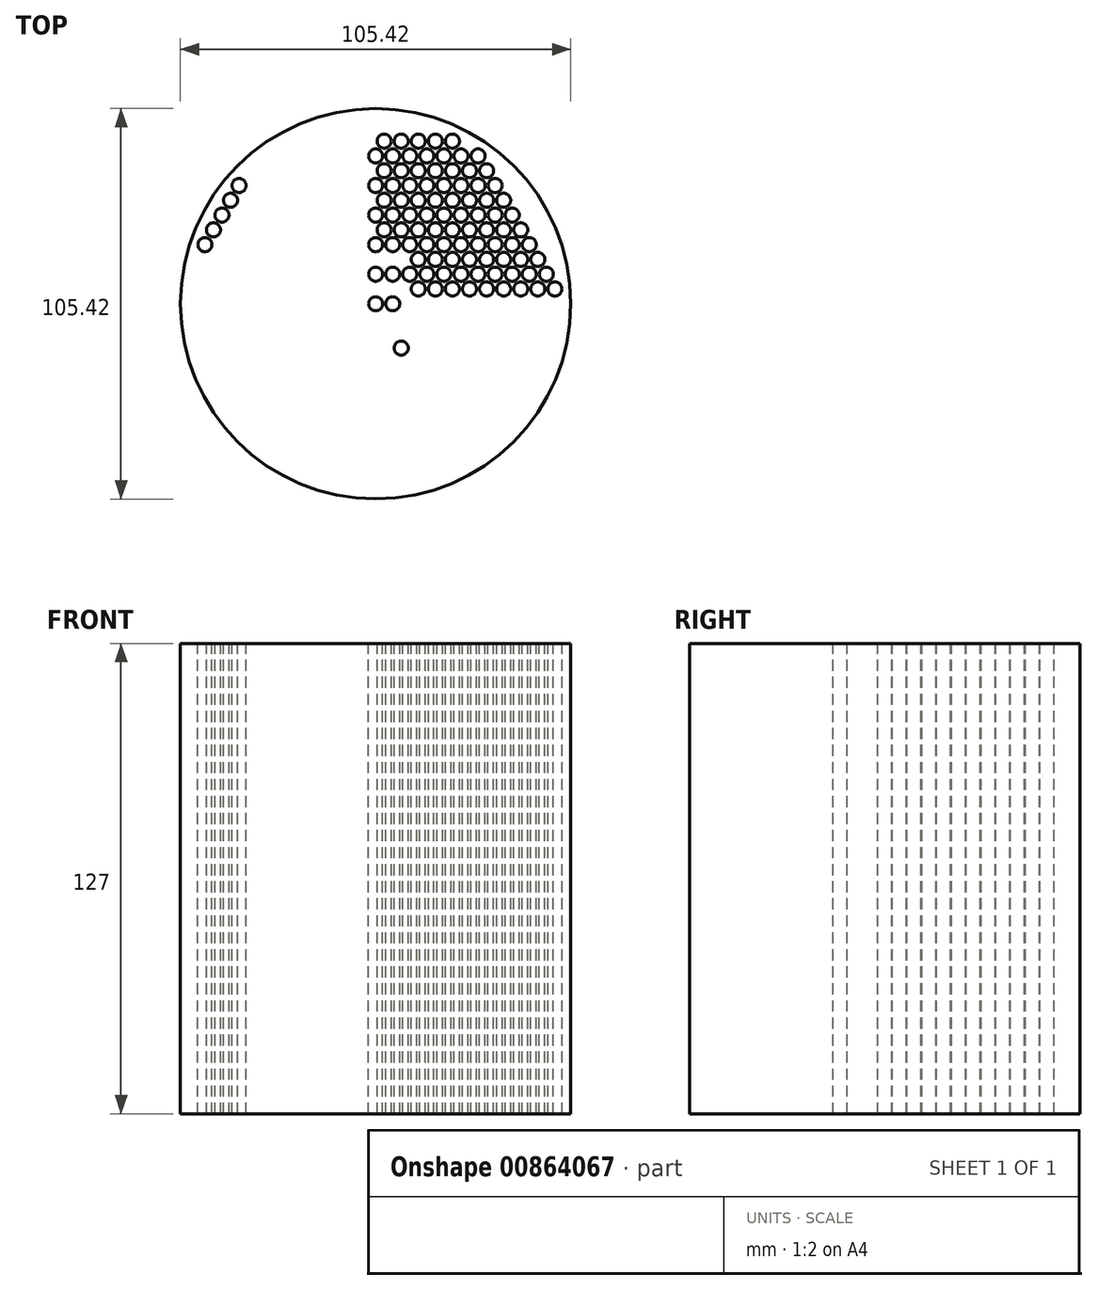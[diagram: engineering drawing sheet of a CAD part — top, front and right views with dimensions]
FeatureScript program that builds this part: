
annotation { "Feature Type Name" : "Feature", "Feature Type Description" : "" }
export const myFeature = defineFeature(function(context is Context, id is Id, definition is map)
    precondition{}
    {
        {
            var Q0;
            Q0=qCreatedBy(makeId("Top.planeOp"),FACE);
            var sketch = newSketch(context, id + "F0", { "sketchPlane" : qUnion([Q0])});
            skCircle(sketch, "E0", {"center": v(0, 0) * mm, "radius": 52.7 * mm});
            skSolve(sketch);
        }
        {
            var Q0;
            Q0=makeQuery(id+"F0.imprint","IMPRINT",FACE,{"disambiguationData":[TD([[makeQuery(id+"F0.imprint","IMPRINT",EDGE,{"derivedFrom":sQuery(id+"F0.wireOp",EDGE,"E0")}),1.0]])]});
            extrude(context, id + "F1", {"entities" : qUnion([Q0]), "depth" : 127 * mm, "offsetDistance" : 25.4 * mm});
        }
        {
            var Q0;
            Q0=makeQuery(id+"F1.opExtrude","CAP_FACE",FACE,{"disambiguationData":[OSD([sQuery(id+"F0.wireOp",EDGE,"E0")])],"isStart":false});
            var sketch = newSketch(context, id + "F2", { "sketchPlane" : qUnion([Q0])});
            skCircle(sketch, "E1", {"center": v(0, 0) * mm, "radius": 50.8 * mm});
            skCircle(sketch, "E2", {"center": v(0, 0) * mm, "radius": 1.9 * mm});
            skSolve(sketch);
        }
        {
            var Q0;
            Q0=makeQuery(id+"F2.imprint","IMPRINT",FACE,{"disambiguationData":[TD([[makeQuery(id+"F2.imprint","IMPRINT",EDGE,{"derivedFrom":sQuery(id+"F2.wireOp",EDGE,"E2")}),1.0]])]});
            var Q1;
            Q1=makeQuery(id+"F1.opExtrude","CAP_FACE",FACE,{"disambiguationData":[OSD([sQuery(id+"F0.wireOp",EDGE,"E0")])],"isStart":true});
            extrude(context, id + "F3", {"entities" : qUnion([Q0]), "operationType" : NewBodyOperationType.REMOVE, "endBound" : BoundingType.UP_TO_SURFACE, "oppositeDirection" : true, "depth" : 25.4 * mm, "endBoundEntityFace" : qUnion([Q1]), "offsetDistance" : 25.4 * mm});
        }
        {
            var Q0;
            Q0=makeQuery(id+"F1.opExtrude","CAP_FACE",FACE,{"disambiguationData":[OSD([sQuery(id+"F0.wireOp",EDGE,"E0")])],"isStart":false});
            var sketch = newSketch(context, id + "F4", { "sketchPlane" : qUnion([Q0])});
            skLineSegment(sketch, "E3", {"start": v(0, 0) * mm, "end": v(52.7, 0) * mm});
            skCircle(sketch, "E4", {"center": v(4.6, 0) * mm, "radius": 1.9 * mm});
            skSolve(sketch);
        }
        {
            var Q0;
            Q0=qCreatedBy(makeId("Front.planeOp"),FACE);
            var sketch = newSketch(context, id + "F5", { "sketchPlane" : qUnion([Q0])});
            skLineSegment(sketch, "E5", {"start": v(0, 162.67) * mm, "end": v(0, -94.61) * mm});
            skSolve(sketch);
        }
        {
            var Q0;
            {var subQ0=sQuery(id+"F4.wireOp",EDGE,"E4");var subQ1=sQuery(id+"F4.wireOp",EDGE,"E3");var subQ2=makeQuery(id+"F4.imprint","INTERSECT",VERTEX,{"disambiguationData":[OD(0.0)],"derivedFrom":[subQ1,subQ0]});Q0=makeQuery(id+"F4.imprint","IMPRINT",FACE,{"disambiguationData":[TD([[makeQuery(id+"F4.imprint","IMPRINT",EDGE,{"disambiguationData":[TD([[subQ2,-1.0]])],"derivedFrom":subQ1}),1.0]])]});}
            var Q1;
            {var subQ0=sQuery(id+"F4.wireOp",EDGE,"E4");var subQ1=sQuery(id+"F4.wireOp",EDGE,"E3");var subQ2=makeQuery(id+"F4.imprint","INTERSECT",VERTEX,{"disambiguationData":[OD(0.0)],"derivedFrom":[subQ1,subQ0]});Q1=makeQuery(id+"F4.imprint","IMPRINT",FACE,{"disambiguationData":[TD([[makeQuery(id+"F4.imprint","IMPRINT",EDGE,{"disambiguationData":[TD([[subQ2,-1.0]])],"derivedFrom":subQ1}),-1.0]])]});}
            var Q2;
            Q2=makeQuery(id+"F1.opExtrude","CAP_FACE",FACE,{"disambiguationData":[OSD([sQuery(id+"F0.wireOp",EDGE,"E0")])],"isStart":true});
            extrude(context, id + "F6", {"entities" : qUnion([Q0, Q1]), "operationType" : NewBodyOperationType.REMOVE, "endBound" : BoundingType.UP_TO_SURFACE, "oppositeDirection" : true, "depth" : 25.4 * mm, "endBoundEntityFace" : qUnion([Q2]), "offsetDistance" : 25.4 * mm});
        }
        {
            var Q0;
            Q0=makeQuery(id+"F1.opExtrude","CAP_FACE",FACE,{"disambiguationData":[OSD([sQuery(id+"F0.wireOp",EDGE,"E0")])],"isStart":false});
            var sketch = newSketch(context, id + "F7", { "sketchPlane" : qUnion([Q0])});
            skLineSegment(sketch, "E6", {"start": v(0, 0) * mm, "end": v(0, 7.98) * mm});
            skCircle(sketch, "E7", {"center": v(0, 7.98) * mm, "radius": 1.9 * mm});
            skSolve(sketch);
        }
        {
            var Q0;
            Q0=makeQuery(id+"F7.imprint","IMPRINT",FACE,{"disambiguationData":[TD([[makeQuery(id+"F7.imprint","IMPRINT",EDGE,{"derivedFrom":sQuery(id+"F7.wireOp",EDGE,"E7")}),1.0]])]});
            var Q1;
            Q1=makeQuery(id+"F1.opExtrude","CAP_FACE",FACE,{"disambiguationData":[OSD([sQuery(id+"F0.wireOp",EDGE,"E0")])],"isStart":true});
            extrude(context, id + "F8", {"entities" : qUnion([Q0]), "operationType" : NewBodyOperationType.REMOVE, "endBound" : BoundingType.UP_TO_SURFACE, "oppositeDirection" : true, "depth" : 25.4 * mm, "endBoundEntityFace" : qUnion([Q1]), "offsetDistance" : 25.4 * mm});
        }
        {
            var Q0;
            Q0=makeQuery(id+"F1.opExtrude","CAP_FACE",FACE,{"disambiguationData":[OSD([sQuery(id+"F0.wireOp",EDGE,"E0")])],"isStart":false});
            var sketch = newSketch(context, id + "F9", { "sketchPlane" : qUnion([Q0])});
            skLineSegment(sketch, "E8", {"start": v(0, 0) * mm, "end": v(8.77, 15.2) * mm});
            skCircle(sketch, "E9", {"center": v(4.61, 7.98) * mm, "radius": 1.9 * mm});
            skSolve(sketch);
        }
        {
            var Q0;
            {var subQ0=sQuery(id+"F9.wireOp",EDGE,"E9");var subQ1=sQuery(id+"F9.wireOp",EDGE,"E8");var subQ2=makeQuery(id+"F9.imprint","INTERSECT",VERTEX,{"disambiguationData":[OD(0.0)],"derivedFrom":[subQ1,subQ0]});Q0=makeQuery(id+"F9.imprint","IMPRINT",FACE,{"disambiguationData":[TD([[makeQuery(id+"F9.imprint","IMPRINT",EDGE,{"disambiguationData":[TD([[subQ2,-1.0]])],"derivedFrom":subQ1}),-1.0]])]});}
            var Q1;
            {var subQ0=sQuery(id+"F9.wireOp",EDGE,"E9");var subQ1=sQuery(id+"F9.wireOp",EDGE,"E8");var subQ2=makeQuery(id+"F9.imprint","INTERSECT",VERTEX,{"disambiguationData":[OD(0.0)],"derivedFrom":[subQ1,subQ0]});Q1=makeQuery(id+"F9.imprint","IMPRINT",FACE,{"disambiguationData":[TD([[makeQuery(id+"F9.imprint","IMPRINT",EDGE,{"disambiguationData":[TD([[subQ2,-1.0]])],"derivedFrom":subQ1}),1.0]])]});}
            var Q2;
            Q2=makeQuery(id+"F1.opExtrude","CAP_FACE",FACE,{"disambiguationData":[OSD([sQuery(id+"F0.wireOp",EDGE,"E0")])],"isStart":true});
            extrude(context, id + "F10", {"entities" : qUnion([Q0, Q1]), "operationType" : NewBodyOperationType.REMOVE, "endBound" : BoundingType.UP_TO_SURFACE, "oppositeDirection" : true, "depth" : 25.4 * mm, "endBoundEntityFace" : qUnion([Q2]), "offsetDistance" : 25.4 * mm});
        }
        {
            var Q0;
            Q0=makeQuery(id+"F1.opExtrude","CAP_FACE",FACE,{"disambiguationData":[OSD([sQuery(id+"F0.wireOp",EDGE,"E0")])],"isStart":false});
            var sketch = newSketch(context, id + "F11", { "sketchPlane" : qUnion([Q0])});
            skLineSegment(sketch, "E10", {"start": v(0, 0) * mm, "end": v(9.22, 7.98) * mm});
            skCircle(sketch, "E11", {"center": v(9.22, 7.98) * mm, "radius": 1.9 * mm});
            skSolve(sketch);
        }
        {
            var Q0;
            Q0=makeQuery(id+"F11.imprint","IMPRINT",FACE,{"disambiguationData":[TD([[makeQuery(id+"F11.imprint","IMPRINT",EDGE,{"derivedFrom":sQuery(id+"F11.wireOp",EDGE,"E11")}),1.0]])]});
            var Q1;
            Q1=makeQuery(id+"F1.opExtrude","CAP_FACE",FACE,{"disambiguationData":[OSD([sQuery(id+"F0.wireOp",EDGE,"E0")])],"isStart":true});
            extrude(context, id + "F12", {"entities" : qUnion([Q0]), "operationType" : NewBodyOperationType.REMOVE, "endBound" : BoundingType.UP_TO_SURFACE, "oppositeDirection" : true, "depth" : 25.4 * mm, "endBoundEntityFace" : qUnion([Q1]), "offsetDistance" : 25.4 * mm});
        }
        {
            var Q0;
            Q0=makeQuery(id+"F1.opExtrude","CAP_FACE",FACE,{"disambiguationData":[OSD([sQuery(id+"F0.wireOp",EDGE,"E0")])],"isStart":false});
            var sketch = newSketch(context, id + "F13", { "sketchPlane" : qUnion([Q0])});
            skLineSegment(sketch, "E12", {"start": v(0, 0) * mm, "end": v(11.53, 4) * mm});
            skCircle(sketch, "E13", {"center": v(11.53, 4) * mm, "radius": 1.9 * mm});
            skSolve(sketch);
        }
        {
            var Q0;
            Q0=makeQuery(id+"F13.imprint","IMPRINT",FACE,{"disambiguationData":[TD([[makeQuery(id+"F13.imprint","IMPRINT",EDGE,{"derivedFrom":sQuery(id+"F13.wireOp",EDGE,"E13")}),1.0]])]});
            var Q1;
            Q1=makeQuery(id+"F1.opExtrude","CAP_FACE",FACE,{"disambiguationData":[OSD([sQuery(id+"F0.wireOp",EDGE,"E0")])],"isStart":true});
            extrude(context, id + "F14", {"entities" : qUnion([Q0]), "operationType" : NewBodyOperationType.REMOVE, "endBound" : BoundingType.UP_TO_SURFACE, "oppositeDirection" : true, "depth" : 25.4 * mm, "endBoundEntityFace" : qUnion([Q1]), "offsetDistance" : 25.4 * mm});
        }
        {
            var Q0;
            Q0=makeQuery(id+"F1.opExtrude","CAP_FACE",FACE,{"disambiguationData":[OSD([sQuery(id+"F0.wireOp",EDGE,"E0")])],"isStart":false});
            var sketch = newSketch(context, id + "F15", { "sketchPlane" : qUnion([Q0])});
            skLineSegment(sketch, "E14", {"start": v(0, 0) * mm, "end": v(6.92, -11.98) * mm});
            skCircle(sketch, "E15", {"center": v(6.92, -11.98) * mm, "radius": 1.9 * mm});
            skSolve(sketch);
        }
        {
            var Q0;
            Q0=makeQuery(id+"F15.imprint","IMPRINT",FACE,{"disambiguationData":[TD([[makeQuery(id+"F15.imprint","IMPRINT",EDGE,{"derivedFrom":sQuery(id+"F15.wireOp",EDGE,"E15")}),1.0]])]});
            var Q1;
            Q1=makeQuery(id+"F1.opExtrude","CAP_FACE",FACE,{"disambiguationData":[OSD([sQuery(id+"F0.wireOp",EDGE,"E0")])],"isStart":true});
            extrude(context, id + "F16", {"entities" : qUnion([Q0]), "operationType" : NewBodyOperationType.REMOVE, "endBound" : BoundingType.UP_TO_SURFACE, "oppositeDirection" : true, "depth" : 25.4 * mm, "endBoundEntityFace" : qUnion([Q1]), "offsetDistance" : 25.4 * mm});
        }
        {
            var Q0;
            Q0=makeQuery(id+"F1.opExtrude","CAP_FACE",FACE,{"disambiguationData":[OSD([sQuery(id+"F0.wireOp",EDGE,"E0")])],"isStart":false});
            var sketch = newSketch(context, id + "F17", { "sketchPlane" : qUnion([Q0])});
            skLineSegment(sketch, "E16", {"start": v(0, 0) * mm, "end": v(0, 15.97) * mm});
            skLineSegment(sketch, "E17", {"start": v(0, 0) * mm, "end": v(4.6, 15.97) * mm});
            skCircle(sketch, "E18", {"center": v(0, 15.97) * mm, "radius": 1.9 * mm});
            skCircle(sketch, "E19", {"center": v(4.6, 15.97) * mm, "radius": 1.9 * mm});
            skLineSegment(sketch, "E20", {"start": v(0, 0) * mm, "end": v(9.22, 15.97) * mm});
            skCircle(sketch, "E21", {"center": v(9.22, 15.97) * mm, "radius": 1.9 * mm});
            skLineSegment(sketch, "E22", {"start": v(0, 0) * mm, "end": v(11.52, 11.98) * mm});
            skCircle(sketch, "E23", {"center": v(11.52, 11.98) * mm, "radius": 1.9 * mm});
            skLineSegment(sketch, "E24", {"start": v(0, 0) * mm, "end": v(13.83, 7.98) * mm});
            skCircle(sketch, "E25", {"center": v(13.83, 7.98) * mm, "radius": 1.9 * mm});
            skLineSegment(sketch, "E26", {"start": v(0, 0) * mm, "end": v(16.14, 4) * mm});
            skCircle(sketch, "E27", {"center": v(16.14, 4) * mm, "radius": 1.9 * mm});
            skSolve(sketch);
        }
        {
            var Q0;
            Q0=makeQuery(id+"F17.imprint","IMPRINT",FACE,{"disambiguationData":[TD([[makeQuery(id+"F17.imprint","IMPRINT",EDGE,{"derivedFrom":sQuery(id+"F17.wireOp",EDGE,"E18")}),1.0]])]});
            var Q1;
            Q1=makeQuery(id+"F17.imprint","IMPRINT",FACE,{"disambiguationData":[TD([[makeQuery(id+"F17.imprint","IMPRINT",EDGE,{"derivedFrom":sQuery(id+"F17.wireOp",EDGE,"E19")}),1.0]])]});
            var Q2;
            Q2=makeQuery(id+"F17.imprint","IMPRINT",FACE,{"disambiguationData":[TD([[makeQuery(id+"F17.imprint","IMPRINT",EDGE,{"derivedFrom":sQuery(id+"F17.wireOp",EDGE,"E21")}),1.0]])]});
            var Q3;
            Q3=makeQuery(id+"F17.imprint","IMPRINT",FACE,{"disambiguationData":[TD([[makeQuery(id+"F17.imprint","IMPRINT",EDGE,{"derivedFrom":sQuery(id+"F17.wireOp",EDGE,"E23")}),1.0]])]});
            var Q4;
            Q4=makeQuery(id+"F17.imprint","IMPRINT",FACE,{"disambiguationData":[TD([[makeQuery(id+"F17.imprint","IMPRINT",EDGE,{"derivedFrom":sQuery(id+"F17.wireOp",EDGE,"E25")}),1.0]])]});
            var Q5;
            Q5=makeQuery(id+"F17.imprint","IMPRINT",FACE,{"disambiguationData":[TD([[makeQuery(id+"F17.imprint","IMPRINT",EDGE,{"derivedFrom":sQuery(id+"F17.wireOp",EDGE,"E27")}),1.0]])]});
            var Q6;
            Q6=makeQuery(id+"F1.opExtrude","CAP_FACE",FACE,{"disambiguationData":[OSD([sQuery(id+"F0.wireOp",EDGE,"E0")])],"isStart":true});
            extrude(context, id + "F18", {"entities" : qUnion([Q0, Q1, Q2, Q3, Q4, Q5]), "operationType" : NewBodyOperationType.REMOVE, "endBound" : BoundingType.UP_TO_SURFACE, "oppositeDirection" : true, "depth" : 25.4 * mm, "endBoundEntityFace" : qUnion([Q6]), "offsetDistance" : 25.4 * mm});
        }
        {
            var Q0;
            Q0=makeQuery(id+"F1.opExtrude","CAP_FACE",FACE,{"disambiguationData":[OSD([sQuery(id+"F0.wireOp",EDGE,"E0")])],"isStart":false});
            var sketch = newSketch(context, id + "F19", { "sketchPlane" : qUnion([Q0])});
            skLineSegment(sketch, "E28", {"start": v(0, 0) * mm, "end": v(2.3, 19.96) * mm});
            skCircle(sketch, "E29", {"center": v(2.3, 19.96) * mm, "radius": 1.9 * mm});
            skLineSegment(sketch, "E30", {"start": v(0, 0) * mm, "end": v(6.91, 19.96) * mm});
            skCircle(sketch, "E31", {"center": v(6.91, 19.96) * mm, "radius": 1.9 * mm});
            skLineSegment(sketch, "E32", {"start": v(0, 0) * mm, "end": v(11.52, 19.96) * mm});
            skCircle(sketch, "E33", {"center": v(11.52, 19.96) * mm, "radius": 1.9 * mm});
            skLineSegment(sketch, "E34", {"start": v(0, 0) * mm, "end": v(13.83, 15.97) * mm});
            skCircle(sketch, "E35", {"center": v(13.83, 15.97) * mm, "radius": 1.9 * mm});
            skLineSegment(sketch, "E36", {"start": v(0, 0) * mm, "end": v(16.13, 11.98) * mm});
            skCircle(sketch, "E37", {"center": v(16.13, 11.98) * mm, "radius": 1.9 * mm});
            skLineSegment(sketch, "E38", {"start": v(0, 0) * mm, "end": v(18.44, 7.98) * mm});
            skCircle(sketch, "E39", {"center": v(18.44, 7.98) * mm, "radius": 1.9 * mm});
            skLineSegment(sketch, "E40", {"start": v(0, 0) * mm, "end": v(20.75, 4) * mm});
            skCircle(sketch, "E41", {"center": v(20.75, 4) * mm, "radius": 1.9 * mm});
            skSolve(sketch);
        }
        {
            var Q0;
            Q0=makeQuery(id+"F19.imprint","IMPRINT",FACE,{"disambiguationData":[TD([[makeQuery(id+"F19.imprint","IMPRINT",EDGE,{"derivedFrom":sQuery(id+"F19.wireOp",EDGE,"E29")}),1.0]])]});
            var Q1;
            Q1=makeQuery(id+"F19.imprint","IMPRINT",FACE,{"disambiguationData":[TD([[makeQuery(id+"F19.imprint","IMPRINT",EDGE,{"derivedFrom":sQuery(id+"F19.wireOp",EDGE,"E31")}),1.0]])]});
            var Q2;
            Q2=makeQuery(id+"F19.imprint","IMPRINT",FACE,{"disambiguationData":[TD([[makeQuery(id+"F19.imprint","IMPRINT",EDGE,{"derivedFrom":sQuery(id+"F19.wireOp",EDGE,"E33")}),1.0]])]});
            var Q3;
            Q3=makeQuery(id+"F19.imprint","IMPRINT",FACE,{"disambiguationData":[TD([[makeQuery(id+"F19.imprint","IMPRINT",EDGE,{"derivedFrom":sQuery(id+"F19.wireOp",EDGE,"E35")}),1.0]])]});
            var Q4;
            Q4=makeQuery(id+"F19.imprint","IMPRINT",FACE,{"disambiguationData":[TD([[makeQuery(id+"F19.imprint","IMPRINT",EDGE,{"derivedFrom":sQuery(id+"F19.wireOp",EDGE,"E37")}),1.0]])]});
            var Q5;
            Q5=makeQuery(id+"F19.imprint","IMPRINT",FACE,{"disambiguationData":[TD([[makeQuery(id+"F19.imprint","IMPRINT",EDGE,{"derivedFrom":sQuery(id+"F19.wireOp",EDGE,"E39")}),1.0]])]});
            var Q6;
            Q6=makeQuery(id+"F19.imprint","IMPRINT",FACE,{"disambiguationData":[TD([[makeQuery(id+"F19.imprint","IMPRINT",EDGE,{"derivedFrom":sQuery(id+"F19.wireOp",EDGE,"E41")}),1.0]])]});
            var Q7;
            Q7=makeQuery(id+"F1.opExtrude","CAP_FACE",FACE,{"disambiguationData":[OSD([sQuery(id+"F0.wireOp",EDGE,"E0")])],"isStart":true});
            extrude(context, id + "F20", {"entities" : qUnion([Q0, Q1, Q2, Q3, Q4, Q5, Q6]), "operationType" : NewBodyOperationType.REMOVE, "endBound" : BoundingType.UP_TO_SURFACE, "oppositeDirection" : true, "depth" : 25.4 * mm, "endBoundEntityFace" : qUnion([Q7]), "offsetDistance" : 25.4 * mm});
        }
        {
            var Q0;
            Q0=makeQuery(id+"F1.opExtrude","CAP_FACE",FACE,{"disambiguationData":[OSD([sQuery(id+"F0.wireOp",EDGE,"E0")])],"isStart":false});
            var sketch = newSketch(context, id + "F21", { "sketchPlane" : qUnion([Q0])});
            skLineSegment(sketch, "E42", {"start": v(0, 0) * mm, "end": v(0, 23.95) * mm});
            skLineSegment(sketch, "E43", {"start": v(0, 0) * mm, "end": v(4.6, 23.95) * mm});
            skLineSegment(sketch, "E44", {"start": v(0, 0) * mm, "end": v(9.22, 23.95) * mm});
            skCircle(sketch, "E45", {"center": v(0, 23.95) * mm, "radius": 1.9 * mm});
            skCircle(sketch, "E46", {"center": v(4.6, 23.95) * mm, "radius": 1.9 * mm});
            skCircle(sketch, "E47", {"center": v(9.22, 23.95) * mm, "radius": 1.9 * mm});
            skLineSegment(sketch, "E48", {"start": v(0, 0) * mm, "end": v(13.83, 23.95) * mm});
            skLineSegment(sketch, "E49", {"start": v(0, 0) * mm, "end": v(16.13, 19.96) * mm});
            skLineSegment(sketch, "E50", {"start": v(0, 0) * mm, "end": v(18.44, 15.97) * mm});
            skLineSegment(sketch, "E51", {"start": v(0, 0) * mm, "end": v(20.74, 11.98) * mm});
            skLineSegment(sketch, "E52", {"start": v(0, 0) * mm, "end": v(23.05, 7.98) * mm});
            skLineSegment(sketch, "E53", {"start": v(0, 0) * mm, "end": v(25.36, 4) * mm});
            skCircle(sketch, "E54", {"center": v(13.83, 23.95) * mm, "radius": 1.9 * mm});
            skCircle(sketch, "E55", {"center": v(16.13, 19.96) * mm, "radius": 1.9 * mm});
            skCircle(sketch, "E56", {"center": v(18.44, 15.97) * mm, "radius": 1.9 * mm});
            skCircle(sketch, "E57", {"center": v(20.74, 11.98) * mm, "radius": 1.9 * mm});
            skCircle(sketch, "E58", {"center": v(23.05, 7.98) * mm, "radius": 1.9 * mm});
            skCircle(sketch, "E59", {"center": v(25.36, 4) * mm, "radius": 1.9 * mm});
            skSolve(sketch);
        }
        {
            var Q0;
            Q0=makeQuery(id+"F21.imprint","IMPRINT",FACE,{"disambiguationData":[TD([[makeQuery(id+"F21.imprint","IMPRINT",EDGE,{"derivedFrom":sQuery(id+"F21.wireOp",EDGE,"E45")}),1.0]])]});
            var Q1;
            Q1=makeQuery(id+"F21.imprint","IMPRINT",FACE,{"disambiguationData":[TD([[makeQuery(id+"F21.imprint","IMPRINT",EDGE,{"derivedFrom":sQuery(id+"F21.wireOp",EDGE,"E46")}),1.0]])]});
            var Q2;
            Q2=makeQuery(id+"F21.imprint","IMPRINT",FACE,{"disambiguationData":[TD([[makeQuery(id+"F21.imprint","IMPRINT",EDGE,{"derivedFrom":sQuery(id+"F21.wireOp",EDGE,"E47")}),1.0]])]});
            var Q3;
            Q3=makeQuery(id+"F21.imprint","IMPRINT",FACE,{"disambiguationData":[TD([[makeQuery(id+"F21.imprint","IMPRINT",EDGE,{"derivedFrom":sQuery(id+"F21.wireOp",EDGE,"E54")}),1.0]])]});
            var Q4;
            Q4=makeQuery(id+"F21.imprint","IMPRINT",FACE,{"disambiguationData":[TD([[makeQuery(id+"F21.imprint","IMPRINT",EDGE,{"derivedFrom":sQuery(id+"F21.wireOp",EDGE,"E55")}),1.0]])]});
            var Q5;
            Q5=makeQuery(id+"F21.imprint","IMPRINT",FACE,{"disambiguationData":[TD([[makeQuery(id+"F21.imprint","IMPRINT",EDGE,{"derivedFrom":sQuery(id+"F21.wireOp",EDGE,"E56")}),1.0]])]});
            var Q6;
            Q6=makeQuery(id+"F21.imprint","IMPRINT",FACE,{"disambiguationData":[TD([[makeQuery(id+"F21.imprint","IMPRINT",EDGE,{"derivedFrom":sQuery(id+"F21.wireOp",EDGE,"E57")}),1.0]])]});
            var Q7;
            Q7=makeQuery(id+"F21.imprint","IMPRINT",FACE,{"disambiguationData":[TD([[makeQuery(id+"F21.imprint","IMPRINT",EDGE,{"derivedFrom":sQuery(id+"F21.wireOp",EDGE,"E58")}),1.0]])]});
            var Q8;
            Q8=makeQuery(id+"F21.imprint","IMPRINT",FACE,{"disambiguationData":[TD([[makeQuery(id+"F21.imprint","IMPRINT",EDGE,{"derivedFrom":sQuery(id+"F21.wireOp",EDGE,"E59")}),1.0]])]});
            var Q9;
            Q9=makeQuery(id+"F1.opExtrude","CAP_FACE",FACE,{"disambiguationData":[OSD([sQuery(id+"F0.wireOp",EDGE,"E0")])],"isStart":true});
            extrude(context, id + "F22", {"entities" : qUnion([Q0, Q1, Q2, Q3, Q4, Q5, Q6, Q7, Q8]), "operationType" : NewBodyOperationType.REMOVE, "endBound" : BoundingType.UP_TO_SURFACE, "oppositeDirection" : true, "depth" : 25.4 * mm, "endBoundEntityFace" : qUnion([Q9]), "offsetDistance" : 25.4 * mm});
        }
        {
            var Q0;
            Q0=makeQuery(id+"F1.opExtrude","CAP_FACE",FACE,{"disambiguationData":[OSD([sQuery(id+"F0.wireOp",EDGE,"E0")])],"isStart":false});
            var sketch = newSketch(context, id + "F23", { "sketchPlane" : qUnion([Q0])});
            skLineSegment(sketch, "E60", {"start": v(0, 0) * mm, "end": v(2.3, 27.95) * mm});
            skLineSegment(sketch, "E61", {"start": v(0, 0) * mm, "end": v(6.91, 27.95) * mm});
            skLineSegment(sketch, "E62", {"start": v(0, 0) * mm, "end": v(11.52, 27.95) * mm});
            skLineSegment(sketch, "E63", {"start": v(0, 0) * mm, "end": v(16.13, 27.95) * mm});
            skCircle(sketch, "E64", {"center": v(2.3, 27.95) * mm, "radius": 1.9 * mm});
            skCircle(sketch, "E65", {"center": v(6.91, 27.95) * mm, "radius": 1.9 * mm});
            skCircle(sketch, "E66", {"center": v(11.52, 27.95) * mm, "radius": 1.9 * mm});
            skCircle(sketch, "E67", {"center": v(16.13, 27.95) * mm, "radius": 1.9 * mm});
            skLineSegment(sketch, "E68", {"start": v(0, 0) * mm, "end": v(18.44, 23.95) * mm});
            skLineSegment(sketch, "E69", {"start": v(0, 0) * mm, "end": v(20.74, 19.96) * mm});
            skLineSegment(sketch, "E70", {"start": v(0, 0) * mm, "end": v(23.05, 15.97) * mm});
            skLineSegment(sketch, "E71", {"start": v(0, 0) * mm, "end": v(25.35, 11.98) * mm});
            skLineSegment(sketch, "E72", {"start": v(0, 0) * mm, "end": v(27.66, 7.98) * mm});
            skLineSegment(sketch, "E73", {"start": v(0, 0) * mm, "end": v(29.97, 4) * mm});
            skCircle(sketch, "E74", {"center": v(20.74, 19.96) * mm, "radius": 1.9 * mm});
            skCircle(sketch, "E75", {"center": v(23.05, 15.97) * mm, "radius": 1.9 * mm});
            skCircle(sketch, "E76", {"center": v(25.35, 11.98) * mm, "radius": 1.9 * mm});
            skCircle(sketch, "E77", {"center": v(27.66, 7.98) * mm, "radius": 1.9 * mm});
            skCircle(sketch, "E78", {"center": v(29.97, 4) * mm, "radius": 1.9 * mm});
            skCircle(sketch, "E79", {"center": v(18.44, 23.95) * mm, "radius": 1.9 * mm});
            skSolve(sketch);
        }
        {
            var Q0;
            Q0=makeQuery(id+"F23.imprint","IMPRINT",FACE,{"disambiguationData":[TD([[makeQuery(id+"F23.imprint","IMPRINT",EDGE,{"derivedFrom":sQuery(id+"F23.wireOp",EDGE,"E64")}),1.0]])]});
            var Q1;
            Q1=makeQuery(id+"F23.imprint","IMPRINT",FACE,{"disambiguationData":[TD([[makeQuery(id+"F23.imprint","IMPRINT",EDGE,{"derivedFrom":sQuery(id+"F23.wireOp",EDGE,"E65")}),1.0]])]});
            var Q2;
            Q2=makeQuery(id+"F23.imprint","IMPRINT",FACE,{"disambiguationData":[TD([[makeQuery(id+"F23.imprint","IMPRINT",EDGE,{"derivedFrom":sQuery(id+"F23.wireOp",EDGE,"E66")}),1.0]])]});
            var Q3;
            Q3=makeQuery(id+"F23.imprint","IMPRINT",FACE,{"disambiguationData":[TD([[makeQuery(id+"F23.imprint","IMPRINT",EDGE,{"derivedFrom":sQuery(id+"F23.wireOp",EDGE,"E67")}),1.0]])]});
            var Q4;
            Q4=makeQuery(id+"F23.imprint","IMPRINT",FACE,{"disambiguationData":[TD([[makeQuery(id+"F23.imprint","IMPRINT",EDGE,{"derivedFrom":sQuery(id+"F23.wireOp",EDGE,"E79")}),1.0]])]});
            var Q5;
            Q5=makeQuery(id+"F23.imprint","IMPRINT",FACE,{"disambiguationData":[TD([[makeQuery(id+"F23.imprint","IMPRINT",EDGE,{"derivedFrom":sQuery(id+"F23.wireOp",EDGE,"E74")}),1.0]])]});
            var Q6;
            Q6=makeQuery(id+"F23.imprint","IMPRINT",FACE,{"disambiguationData":[TD([[makeQuery(id+"F23.imprint","IMPRINT",EDGE,{"derivedFrom":sQuery(id+"F23.wireOp",EDGE,"E75")}),1.0]])]});
            var Q7;
            Q7=makeQuery(id+"F23.imprint","IMPRINT",FACE,{"disambiguationData":[TD([[makeQuery(id+"F23.imprint","IMPRINT",EDGE,{"derivedFrom":sQuery(id+"F23.wireOp",EDGE,"E76")}),1.0]])]});
            var Q8;
            Q8=makeQuery(id+"F23.imprint","IMPRINT",FACE,{"disambiguationData":[TD([[makeQuery(id+"F23.imprint","IMPRINT",EDGE,{"derivedFrom":sQuery(id+"F23.wireOp",EDGE,"E77")}),1.0]])]});
            var Q9;
            Q9=makeQuery(id+"F23.imprint","IMPRINT",FACE,{"disambiguationData":[TD([[makeQuery(id+"F23.imprint","IMPRINT",EDGE,{"derivedFrom":sQuery(id+"F23.wireOp",EDGE,"E78")}),1.0]])]});
            var Q10;
            Q10=makeQuery(id+"F1.opExtrude","CAP_FACE",FACE,{"disambiguationData":[OSD([sQuery(id+"F0.wireOp",EDGE,"E0")])],"isStart":true});
            extrude(context, id + "F24", {"entities" : qUnion([Q0, Q1, Q2, Q3, Q4, Q5, Q6, Q7, Q8, Q9]), "operationType" : NewBodyOperationType.REMOVE, "endBound" : BoundingType.UP_TO_SURFACE, "oppositeDirection" : true, "depth" : 25.4 * mm, "endBoundEntityFace" : qUnion([Q10]), "offsetDistance" : 25.4 * mm});
        }
        {
            var Q0;
            Q0=makeQuery(id+"F1.opExtrude","CAP_FACE",FACE,{"disambiguationData":[OSD([sQuery(id+"F0.wireOp",EDGE,"E0")])],"isStart":false});
            var sketch = newSketch(context, id + "F25", { "sketchPlane" : qUnion([Q0])});
            skLineSegment(sketch, "E80", {"start": v(0, 0) * mm, "end": v(0, 31.94) * mm});
            skLineSegment(sketch, "E81", {"start": v(0, 0) * mm, "end": v(4.6, 31.94) * mm});
            skLineSegment(sketch, "E82", {"start": v(0, 0) * mm, "end": v(9.22, 31.94) * mm});
            skLineSegment(sketch, "E83", {"start": v(0, 0) * mm, "end": v(13.83, 31.94) * mm});
            skCircle(sketch, "E84", {"center": v(0, 31.94) * mm, "radius": 1.9 * mm});
            skCircle(sketch, "E85", {"center": v(4.6, 31.94) * mm, "radius": 1.9 * mm});
            skCircle(sketch, "E86", {"center": v(9.22, 31.94) * mm, "radius": 1.9 * mm});
            skCircle(sketch, "E87", {"center": v(13.83, 31.94) * mm, "radius": 1.9 * mm});
            skLineSegment(sketch, "E88", {"start": v(0, 0) * mm, "end": v(18.44, 31.94) * mm});
            skLineSegment(sketch, "E89", {"start": v(0, 0) * mm, "end": v(20.74, 27.95) * mm});
            skLineSegment(sketch, "E90", {"start": v(0, 0) * mm, "end": v(23.05, 23.95) * mm});
            skCircle(sketch, "E91", {"center": v(18.44, 31.94) * mm, "radius": 1.9 * mm});
            skCircle(sketch, "E92", {"center": v(20.74, 27.95) * mm, "radius": 1.9 * mm});
            skCircle(sketch, "E93", {"center": v(23.05, 23.95) * mm, "radius": 1.9 * mm});
            skLineSegment(sketch, "E94", {"start": v(0, 0) * mm, "end": v(25.35, 19.96) * mm});
            skLineSegment(sketch, "E95", {"start": v(0, 0) * mm, "end": v(27.66, 15.97) * mm});
            skLineSegment(sketch, "E96", {"start": v(0, 0) * mm, "end": v(29.96, 11.98) * mm});
            skLineSegment(sketch, "E97", {"start": v(0, 0) * mm, "end": v(32.27, 7.98) * mm});
            skLineSegment(sketch, "E98", {"start": v(0, 0) * mm, "end": v(34.58, 4) * mm});
            skCircle(sketch, "E99", {"center": v(25.35, 19.96) * mm, "radius": 1.9 * mm});
            skCircle(sketch, "E100", {"center": v(27.66, 15.97) * mm, "radius": 1.9 * mm});
            skCircle(sketch, "E101", {"center": v(29.96, 11.98) * mm, "radius": 1.9 * mm});
            skCircle(sketch, "E102", {"center": v(32.27, 7.98) * mm, "radius": 1.9 * mm});
            skCircle(sketch, "E103", {"center": v(34.58, 4) * mm, "radius": 1.9 * mm});
            skSolve(sketch);
        }
        {
            var Q0;
            Q0=makeQuery(id+"F25.imprint","IMPRINT",FACE,{"disambiguationData":[TD([[makeQuery(id+"F25.imprint","IMPRINT",EDGE,{"derivedFrom":sQuery(id+"F25.wireOp",EDGE,"E84")}),1.0]])]});
            var Q1;
            Q1=makeQuery(id+"F25.imprint","IMPRINT",FACE,{"disambiguationData":[TD([[makeQuery(id+"F25.imprint","IMPRINT",EDGE,{"derivedFrom":sQuery(id+"F25.wireOp",EDGE,"E85")}),1.0]])]});
            var Q2;
            Q2=makeQuery(id+"F25.imprint","IMPRINT",FACE,{"disambiguationData":[TD([[makeQuery(id+"F25.imprint","IMPRINT",EDGE,{"derivedFrom":sQuery(id+"F25.wireOp",EDGE,"E86")}),1.0]])]});
            var Q3;
            Q3=makeQuery(id+"F25.imprint","IMPRINT",FACE,{"disambiguationData":[TD([[makeQuery(id+"F25.imprint","IMPRINT",EDGE,{"derivedFrom":sQuery(id+"F25.wireOp",EDGE,"E87")}),1.0]])]});
            var Q4;
            Q4=makeQuery(id+"F25.imprint","IMPRINT",FACE,{"disambiguationData":[TD([[makeQuery(id+"F25.imprint","IMPRINT",EDGE,{"derivedFrom":sQuery(id+"F25.wireOp",EDGE,"E91")}),1.0]])]});
            var Q5;
            Q5=makeQuery(id+"F25.imprint","IMPRINT",FACE,{"disambiguationData":[TD([[makeQuery(id+"F25.imprint","IMPRINT",EDGE,{"derivedFrom":sQuery(id+"F25.wireOp",EDGE,"E92")}),1.0]])]});
            var Q6;
            Q6=makeQuery(id+"F25.imprint","IMPRINT",FACE,{"disambiguationData":[TD([[makeQuery(id+"F25.imprint","IMPRINT",EDGE,{"derivedFrom":sQuery(id+"F25.wireOp",EDGE,"E93")}),1.0]])]});
            var Q7;
            Q7=makeQuery(id+"F25.imprint","IMPRINT",FACE,{"disambiguationData":[TD([[makeQuery(id+"F25.imprint","IMPRINT",EDGE,{"derivedFrom":sQuery(id+"F25.wireOp",EDGE,"E99")}),1.0]])]});
            var Q8;
            Q8=makeQuery(id+"F25.imprint","IMPRINT",FACE,{"disambiguationData":[TD([[makeQuery(id+"F25.imprint","IMPRINT",EDGE,{"derivedFrom":sQuery(id+"F25.wireOp",EDGE,"E100")}),1.0]])]});
            var Q9;
            Q9=makeQuery(id+"F25.imprint","IMPRINT",FACE,{"disambiguationData":[TD([[makeQuery(id+"F25.imprint","IMPRINT",EDGE,{"derivedFrom":sQuery(id+"F25.wireOp",EDGE,"E101")}),1.0]])]});
            var Q10;
            Q10=makeQuery(id+"F25.imprint","IMPRINT",FACE,{"disambiguationData":[TD([[makeQuery(id+"F25.imprint","IMPRINT",EDGE,{"derivedFrom":sQuery(id+"F25.wireOp",EDGE,"E102")}),1.0]])]});
            var Q11;
            Q11=makeQuery(id+"F25.imprint","IMPRINT",FACE,{"disambiguationData":[TD([[makeQuery(id+"F25.imprint","IMPRINT",EDGE,{"derivedFrom":sQuery(id+"F25.wireOp",EDGE,"E103")}),1.0]])]});
            var Q12;
            Q12=makeQuery(id+"F1.opExtrude","CAP_FACE",FACE,{"disambiguationData":[OSD([sQuery(id+"F0.wireOp",EDGE,"E0")])],"isStart":true});
            extrude(context, id + "F26", {"entities" : qUnion([Q0, Q1, Q2, Q3, Q4, Q5, Q6, Q7, Q8, Q9, Q10, Q11]), "operationType" : NewBodyOperationType.REMOVE, "endBound" : BoundingType.UP_TO_SURFACE, "oppositeDirection" : true, "depth" : 25.4 * mm, "endBoundEntityFace" : qUnion([Q12]), "offsetDistance" : 25.4 * mm});
        }
        {
            var Q0;
            Q0=makeQuery(id+"F1.opExtrude","CAP_FACE",FACE,{"disambiguationData":[OSD([sQuery(id+"F0.wireOp",EDGE,"E0")])],"isStart":false});
            var sketch = newSketch(context, id + "F27", { "sketchPlane" : qUnion([Q0])});
            skLineSegment(sketch, "E104", {"start": v(0, 0) * mm, "end": v(2.3, 35.93) * mm});
            skLineSegment(sketch, "E105", {"start": v(6.91, 35.93) * mm, "end": v(0, 0) * mm});
            skLineSegment(sketch, "E106", {"start": v(11.52, 35.93) * mm, "end": v(0, 0) * mm});
            skLineSegment(sketch, "E107", {"start": v(16.13, 35.93) * mm, "end": v(0, 0) * mm});
            skLineSegment(sketch, "E108", {"start": v(20.74, 35.93) * mm, "end": v(0, 0) * mm});
            skLineSegment(sketch, "E109", {"start": v(23.05, 31.94) * mm, "end": v(0, 0) * mm});
            skLineSegment(sketch, "E110", {"start": v(25.35, 27.95) * mm, "end": v(0, 0) * mm});
            skLineSegment(sketch, "E111", {"start": v(27.66, 23.95) * mm, "end": v(0, 0) * mm});
            skLineSegment(sketch, "E112", {"start": v(29.96, 19.96) * mm, "end": v(0, 0) * mm});
            skLineSegment(sketch, "E113", {"start": v(32.27, 15.97) * mm, "end": v(0, 0) * mm});
            skLineSegment(sketch, "E114", {"start": v(34.57, 11.98) * mm, "end": v(0, 0) * mm});
            skLineSegment(sketch, "E115", {"start": v(36.88, 7.98) * mm, "end": v(0, 0) * mm});
            skLineSegment(sketch, "E116", {"start": v(39.18, 4) * mm, "end": v(0, 0) * mm});
            skCircle(sketch, "E117", {"center": v(2.3, 35.93) * mm, "radius": 1.9 * mm});
            skCircle(sketch, "E118", {"center": v(6.91, 35.93) * mm, "radius": 1.9 * mm});
            skCircle(sketch, "E119", {"center": v(11.52, 35.93) * mm, "radius": 1.9 * mm});
            skCircle(sketch, "E120", {"center": v(16.13, 35.93) * mm, "radius": 1.9 * mm});
            skCircle(sketch, "E121", {"center": v(20.74, 35.93) * mm, "radius": 1.9 * mm});
            skCircle(sketch, "E122", {"center": v(23.05, 31.94) * mm, "radius": 1.9 * mm});
            skCircle(sketch, "E123", {"center": v(25.35, 27.95) * mm, "radius": 1.9 * mm});
            skCircle(sketch, "E124", {"center": v(27.66, 23.95) * mm, "radius": 1.9 * mm});
            skCircle(sketch, "E125", {"center": v(29.96, 19.96) * mm, "radius": 1.9 * mm});
            skCircle(sketch, "E126", {"center": v(32.27, 15.97) * mm, "radius": 1.9 * mm});
            skCircle(sketch, "E127", {"center": v(34.57, 11.98) * mm, "radius": 1.9 * mm});
            skCircle(sketch, "E128", {"center": v(36.88, 7.98) * mm, "radius": 1.9 * mm});
            skCircle(sketch, "E129", {"center": v(39.18, 4) * mm, "radius": 1.9 * mm});
            skSolve(sketch);
        }
        {
            var Q0;
            Q0=makeQuery(id+"F27.imprint","IMPRINT",FACE,{"disambiguationData":[TD([[makeQuery(id+"F27.imprint","IMPRINT",EDGE,{"derivedFrom":sQuery(id+"F27.wireOp",EDGE,"E117")}),1.0]])]});
            var Q1;
            Q1=makeQuery(id+"F27.imprint","IMPRINT",FACE,{"disambiguationData":[TD([[makeQuery(id+"F27.imprint","IMPRINT",EDGE,{"derivedFrom":sQuery(id+"F27.wireOp",EDGE,"E118")}),1.0]])]});
            var Q2;
            Q2=makeQuery(id+"F27.imprint","IMPRINT",FACE,{"disambiguationData":[TD([[makeQuery(id+"F27.imprint","IMPRINT",EDGE,{"derivedFrom":sQuery(id+"F27.wireOp",EDGE,"E119")}),1.0]])]});
            var Q3;
            Q3=makeQuery(id+"F27.imprint","IMPRINT",FACE,{"disambiguationData":[TD([[makeQuery(id+"F27.imprint","IMPRINT",EDGE,{"derivedFrom":sQuery(id+"F27.wireOp",EDGE,"E120")}),1.0]])]});
            var Q4;
            Q4=makeQuery(id+"F27.imprint","IMPRINT",FACE,{"disambiguationData":[TD([[makeQuery(id+"F27.imprint","IMPRINT",EDGE,{"derivedFrom":sQuery(id+"F27.wireOp",EDGE,"E121")}),1.0]])]});
            var Q5;
            Q5=makeQuery(id+"F27.imprint","IMPRINT",FACE,{"disambiguationData":[TD([[makeQuery(id+"F27.imprint","IMPRINT",EDGE,{"derivedFrom":sQuery(id+"F27.wireOp",EDGE,"E122")}),1.0]])]});
            var Q6;
            Q6=makeQuery(id+"F27.imprint","IMPRINT",FACE,{"disambiguationData":[TD([[makeQuery(id+"F27.imprint","IMPRINT",EDGE,{"derivedFrom":sQuery(id+"F27.wireOp",EDGE,"E123")}),1.0]])]});
            var Q7;
            Q7=makeQuery(id+"F27.imprint","IMPRINT",FACE,{"disambiguationData":[TD([[makeQuery(id+"F27.imprint","IMPRINT",EDGE,{"derivedFrom":sQuery(id+"F27.wireOp",EDGE,"E124")}),1.0]])]});
            var Q8;
            Q8=makeQuery(id+"F27.imprint","IMPRINT",FACE,{"disambiguationData":[TD([[makeQuery(id+"F27.imprint","IMPRINT",EDGE,{"derivedFrom":sQuery(id+"F27.wireOp",EDGE,"E125")}),1.0]])]});
            var Q9;
            Q9=makeQuery(id+"F27.imprint","IMPRINT",FACE,{"disambiguationData":[TD([[makeQuery(id+"F27.imprint","IMPRINT",EDGE,{"derivedFrom":sQuery(id+"F27.wireOp",EDGE,"E126")}),1.0]])]});
            var Q10;
            Q10=makeQuery(id+"F27.imprint","IMPRINT",FACE,{"disambiguationData":[TD([[makeQuery(id+"F27.imprint","IMPRINT",EDGE,{"derivedFrom":sQuery(id+"F27.wireOp",EDGE,"E127")}),1.0]])]});
            var Q11;
            Q11=makeQuery(id+"F27.imprint","IMPRINT",FACE,{"disambiguationData":[TD([[makeQuery(id+"F27.imprint","IMPRINT",EDGE,{"derivedFrom":sQuery(id+"F27.wireOp",EDGE,"E128")}),1.0]])]});
            var Q12;
            Q12=makeQuery(id+"F27.imprint","IMPRINT",FACE,{"disambiguationData":[TD([[makeQuery(id+"F27.imprint","IMPRINT",EDGE,{"derivedFrom":sQuery(id+"F27.wireOp",EDGE,"E129")}),1.0]])]});
            var Q13;
            Q13=makeQuery(id+"F1.opExtrude","CAP_FACE",FACE,{"disambiguationData":[OSD([sQuery(id+"F0.wireOp",EDGE,"E0")])],"isStart":true});
            extrude(context, id + "F28", {"entities" : qUnion([Q0, Q1, Q2, Q3, Q4, Q5, Q6, Q7, Q8, Q9, Q10, Q11, Q12]), "operationType" : NewBodyOperationType.REMOVE, "endBound" : BoundingType.UP_TO_SURFACE, "oppositeDirection" : true, "depth" : 25.4 * mm, "endBoundEntityFace" : qUnion([Q13]), "offsetDistance" : 25.4 * mm});
        }
        {
            var Q0;
            Q0=makeQuery(id+"F1.opExtrude","CAP_FACE",FACE,{"disambiguationData":[OSD([sQuery(id+"F0.wireOp",EDGE,"E0")])],"isStart":false});
            var sketch = newSketch(context, id + "F29", { "sketchPlane" : qUnion([Q0])});
            skLineSegment(sketch, "E130", {"start": v(0, 39.92) * mm, "end": v(0, 0) * mm});
            skLineSegment(sketch, "E131", {"start": v(0, 0) * mm, "end": v(4.6, 39.92) * mm});
            skLineSegment(sketch, "E132", {"start": v(9.22, 39.92) * mm, "end": v(0, 0) * mm});
            skLineSegment(sketch, "E133", {"start": v(13.83, 39.92) * mm, "end": v(0, 0) * mm});
            skLineSegment(sketch, "E134", {"start": v(18.44, 39.92) * mm, "end": v(0, 0) * mm});
            skLineSegment(sketch, "E135", {"start": v(23.05, 39.92) * mm, "end": v(0, 0) * mm});
            skLineSegment(sketch, "E136", {"start": v(25.35, 35.93) * mm, "end": v(0, 0) * mm});
            skLineSegment(sketch, "E137", {"start": v(27.66, 31.94) * mm, "end": v(0, 0) * mm});
            skLineSegment(sketch, "E138", {"start": v(29.96, 27.95) * mm, "end": v(0, 0) * mm});
            skLineSegment(sketch, "E139", {"start": v(32.27, 23.95) * mm, "end": v(0, 0) * mm});
            skLineSegment(sketch, "E140", {"start": v(34.57, 19.96) * mm, "end": v(0, 0) * mm});
            skLineSegment(sketch, "E141", {"start": v(36.88, 15.97) * mm, "end": v(0, 0) * mm});
            skLineSegment(sketch, "E142", {"start": v(39.18, 11.98) * mm, "end": v(0, 0) * mm});
            skLineSegment(sketch, "E143", {"start": v(41.5, 7.98) * mm, "end": v(0, 0) * mm});
            skLineSegment(sketch, "E144", {"start": v(43.8, 4) * mm, "end": v(0, 0) * mm});
            skCircle(sketch, "E145", {"center": v(0, 39.92) * mm, "radius": 1.9 * mm});
            skCircle(sketch, "E146", {"center": v(4.6, 39.92) * mm, "radius": 1.9 * mm});
            skCircle(sketch, "E147", {"center": v(9.22, 39.92) * mm, "radius": 1.9 * mm});
            skCircle(sketch, "E148", {"center": v(13.83, 39.92) * mm, "radius": 1.9 * mm});
            skCircle(sketch, "E149", {"center": v(18.44, 39.92) * mm, "radius": 1.9 * mm});
            skCircle(sketch, "E150", {"center": v(23.05, 39.92) * mm, "radius": 1.9 * mm});
            skCircle(sketch, "E151", {"center": v(25.35, 35.93) * mm, "radius": 1.9 * mm});
            skCircle(sketch, "E152", {"center": v(27.66, 31.94) * mm, "radius": 1.9 * mm});
            skCircle(sketch, "E153", {"center": v(29.96, 27.95) * mm, "radius": 1.9 * mm});
            skCircle(sketch, "E154", {"center": v(32.27, 23.95) * mm, "radius": 1.9 * mm});
            skCircle(sketch, "E155", {"center": v(34.57, 19.96) * mm, "radius": 1.9 * mm});
            skCircle(sketch, "E156", {"center": v(36.88, 15.97) * mm, "radius": 1.9 * mm});
            skCircle(sketch, "E157", {"center": v(39.18, 11.98) * mm, "radius": 1.9 * mm});
            skCircle(sketch, "E158", {"center": v(41.5, 7.98) * mm, "radius": 1.9 * mm});
            skCircle(sketch, "E159", {"center": v(43.8, 4) * mm, "radius": 1.9 * mm});
            skSolve(sketch);
        }
        {
            var Q0;
            Q0=makeQuery(id+"F29.imprint","IMPRINT",FACE,{"disambiguationData":[TD([[makeQuery(id+"F29.imprint","IMPRINT",EDGE,{"derivedFrom":sQuery(id+"F29.wireOp",EDGE,"E145")}),1.0]])]});
            var Q1;
            Q1=makeQuery(id+"F29.imprint","IMPRINT",FACE,{"disambiguationData":[TD([[makeQuery(id+"F29.imprint","IMPRINT",EDGE,{"derivedFrom":sQuery(id+"F29.wireOp",EDGE,"E146")}),1.0]])]});
            var Q2;
            Q2=makeQuery(id+"F29.imprint","IMPRINT",FACE,{"disambiguationData":[TD([[makeQuery(id+"F29.imprint","IMPRINT",EDGE,{"derivedFrom":sQuery(id+"F29.wireOp",EDGE,"E147")}),1.0]])]});
            var Q3;
            Q3=makeQuery(id+"F29.imprint","IMPRINT",FACE,{"disambiguationData":[TD([[makeQuery(id+"F29.imprint","IMPRINT",EDGE,{"derivedFrom":sQuery(id+"F29.wireOp",EDGE,"E148")}),1.0]])]});
            var Q4;
            Q4=makeQuery(id+"F29.imprint","IMPRINT",FACE,{"disambiguationData":[TD([[makeQuery(id+"F29.imprint","IMPRINT",EDGE,{"derivedFrom":sQuery(id+"F29.wireOp",EDGE,"E149")}),1.0]])]});
            var Q5;
            Q5=makeQuery(id+"F29.imprint","IMPRINT",FACE,{"disambiguationData":[TD([[makeQuery(id+"F29.imprint","IMPRINT",EDGE,{"derivedFrom":sQuery(id+"F29.wireOp",EDGE,"E150")}),1.0]])]});
            var Q6;
            Q6=makeQuery(id+"F29.imprint","IMPRINT",FACE,{"disambiguationData":[TD([[makeQuery(id+"F29.imprint","IMPRINT",EDGE,{"derivedFrom":sQuery(id+"F29.wireOp",EDGE,"E151")}),1.0]])]});
            var Q7;
            Q7=makeQuery(id+"F29.imprint","IMPRINT",FACE,{"disambiguationData":[TD([[makeQuery(id+"F29.imprint","IMPRINT",EDGE,{"derivedFrom":sQuery(id+"F29.wireOp",EDGE,"E152")}),1.0]])]});
            var Q8;
            Q8=makeQuery(id+"F29.imprint","IMPRINT",FACE,{"disambiguationData":[TD([[makeQuery(id+"F29.imprint","IMPRINT",EDGE,{"derivedFrom":sQuery(id+"F29.wireOp",EDGE,"E153")}),1.0]])]});
            var Q9;
            Q9=makeQuery(id+"F29.imprint","IMPRINT",FACE,{"disambiguationData":[TD([[makeQuery(id+"F29.imprint","IMPRINT",EDGE,{"derivedFrom":sQuery(id+"F29.wireOp",EDGE,"E154")}),1.0]])]});
            var Q10;
            Q10=makeQuery(id+"F29.imprint","IMPRINT",FACE,{"disambiguationData":[TD([[makeQuery(id+"F29.imprint","IMPRINT",EDGE,{"derivedFrom":sQuery(id+"F29.wireOp",EDGE,"E155")}),1.0]])]});
            var Q11;
            Q11=makeQuery(id+"F29.imprint","IMPRINT",FACE,{"disambiguationData":[TD([[makeQuery(id+"F29.imprint","IMPRINT",EDGE,{"derivedFrom":sQuery(id+"F29.wireOp",EDGE,"E156")}),1.0]])]});
            var Q12;
            Q12=makeQuery(id+"F29.imprint","IMPRINT",FACE,{"disambiguationData":[TD([[makeQuery(id+"F29.imprint","IMPRINT",EDGE,{"derivedFrom":sQuery(id+"F29.wireOp",EDGE,"E157")}),1.0]])]});
            var Q13;
            Q13=makeQuery(id+"F29.imprint","IMPRINT",FACE,{"disambiguationData":[TD([[makeQuery(id+"F29.imprint","IMPRINT",EDGE,{"derivedFrom":sQuery(id+"F29.wireOp",EDGE,"E158")}),1.0]])]});
            var Q14;
            Q14=makeQuery(id+"F29.imprint","IMPRINT",FACE,{"disambiguationData":[TD([[makeQuery(id+"F29.imprint","IMPRINT",EDGE,{"derivedFrom":sQuery(id+"F29.wireOp",EDGE,"E159")}),1.0]])]});
            var Q15;
            Q15=makeQuery(id+"F1.opExtrude","CAP_FACE",FACE,{"disambiguationData":[OSD([sQuery(id+"F0.wireOp",EDGE,"E0")])],"isStart":true});
            extrude(context, id + "F30", {"entities" : qUnion([Q0, Q1, Q2, Q3, Q4, Q5, Q6, Q7, Q8, Q9, Q10, Q11, Q12, Q13, Q14]), "operationType" : NewBodyOperationType.REMOVE, "endBound" : BoundingType.UP_TO_SURFACE, "oppositeDirection" : true, "depth" : 25.4 * mm, "endBoundEntityFace" : qUnion([Q15]), "offsetDistance" : 25.4 * mm});
        }
        {
            var Q0;
            Q0=makeQuery(id+"F1.opExtrude","CAP_FACE",FACE,{"disambiguationData":[OSD([sQuery(id+"F0.wireOp",EDGE,"E0")])],"isStart":false});
            var sketch = newSketch(context, id + "F31", { "sketchPlane" : qUnion([Q0])});
            skLineSegment(sketch, "E160", {"start": v(2.3, 43.92) * mm, "end": v(0, 0) * mm});
            skLineSegment(sketch, "E161", {"start": v(0, 0) * mm, "end": v(6.91, 43.92) * mm});
            skLineSegment(sketch, "E162", {"start": v(11.52, 43.92) * mm, "end": v(0, 0) * mm});
            skLineSegment(sketch, "E163", {"start": v(16.13, 43.92) * mm, "end": v(0, 0) * mm});
            skLineSegment(sketch, "E164", {"start": v(20.74, 43.92) * mm, "end": v(0, 0) * mm});
            skLineSegment(sketch, "E165", {"start": v(27.66, 39.92) * mm, "end": v(0, 0) * mm});
            skLineSegment(sketch, "E166", {"start": v(29.96, 35.93) * mm, "end": v(0, 0) * mm});
            skLineSegment(sketch, "E167", {"start": v(32.27, 31.94) * mm, "end": v(0, 0) * mm});
            skLineSegment(sketch, "E168", {"start": v(34.58, 27.95) * mm, "end": v(0, 0) * mm});
            skLineSegment(sketch, "E169", {"start": v(36.88, 23.95) * mm, "end": v(0, 0) * mm});
            skLineSegment(sketch, "E170", {"start": v(39.19, 19.96) * mm, "end": v(0, 0) * mm});
            skLineSegment(sketch, "E171", {"start": v(41.5, 15.97) * mm, "end": v(0, 0) * mm});
            skLineSegment(sketch, "E172", {"start": v(43.8, 11.98) * mm, "end": v(0, 0) * mm});
            skLineSegment(sketch, "E173", {"start": v(46.1, 7.98) * mm, "end": v(0, 0) * mm});
            skLineSegment(sketch, "E174", {"start": v(48.4, 4) * mm, "end": v(0, 0) * mm});
            skCircle(sketch, "E175", {"center": v(2.3, 43.92) * mm, "radius": 1.9 * mm});
            skCircle(sketch, "E176", {"center": v(6.91, 43.92) * mm, "radius": 1.9 * mm});
            skCircle(sketch, "E177", {"center": v(11.52, 43.92) * mm, "radius": 1.9 * mm});
            skCircle(sketch, "E178", {"center": v(16.13, 43.92) * mm, "radius": 1.9 * mm});
            skCircle(sketch, "E179", {"center": v(20.74, 43.92) * mm, "radius": 1.9 * mm});
            skCircle(sketch, "E180", {"center": v(27.66, 39.92) * mm, "radius": 1.9 * mm});
            skCircle(sketch, "E181", {"center": v(29.96, 35.93) * mm, "radius": 1.9 * mm});
            skCircle(sketch, "E182", {"center": v(32.27, 31.94) * mm, "radius": 1.9 * mm});
            skCircle(sketch, "E183", {"center": v(34.57, 27.95) * mm, "radius": 1.9 * mm});
            skCircle(sketch, "E184", {"center": v(36.88, 23.95) * mm, "radius": 1.9 * mm});
            skCircle(sketch, "E185", {"center": v(39.18, 19.96) * mm, "radius": 1.9 * mm});
            skCircle(sketch, "E186", {"center": v(41.5, 15.97) * mm, "radius": 1.9 * mm});
            skCircle(sketch, "E187", {"center": v(43.8, 11.98) * mm, "radius": 1.9 * mm});
            skCircle(sketch, "E188", {"center": v(46.1, 7.98) * mm, "radius": 1.9 * mm});
            skCircle(sketch, "E189", {"center": v(48.4, 4) * mm, "radius": 1.9 * mm});
            skSolve(sketch);
        }
        {
            var Q0;
            Q0=makeQuery(id+"F31.imprint","IMPRINT",FACE,{"disambiguationData":[TD([[makeQuery(id+"F31.imprint","IMPRINT",EDGE,{"derivedFrom":sQuery(id+"F31.wireOp",EDGE,"E175")}),1.0]])]});
            var Q1;
            Q1=makeQuery(id+"F31.imprint","IMPRINT",FACE,{"disambiguationData":[TD([[makeQuery(id+"F31.imprint","IMPRINT",EDGE,{"derivedFrom":sQuery(id+"F31.wireOp",EDGE,"E176")}),1.0]])]});
            var Q2;
            Q2=makeQuery(id+"F31.imprint","IMPRINT",FACE,{"disambiguationData":[TD([[makeQuery(id+"F31.imprint","IMPRINT",EDGE,{"derivedFrom":sQuery(id+"F31.wireOp",EDGE,"E177")}),1.0]])]});
            var Q3;
            Q3=makeQuery(id+"F31.imprint","IMPRINT",FACE,{"disambiguationData":[TD([[makeQuery(id+"F31.imprint","IMPRINT",EDGE,{"derivedFrom":sQuery(id+"F31.wireOp",EDGE,"E178")}),1.0]])]});
            var Q4;
            Q4=makeQuery(id+"F31.imprint","IMPRINT",FACE,{"disambiguationData":[TD([[makeQuery(id+"F31.imprint","IMPRINT",EDGE,{"derivedFrom":sQuery(id+"F31.wireOp",EDGE,"E179")}),1.0]])]});
            var Q5;
            Q5=makeQuery(id+"F31.imprint","IMPRINT",FACE,{"disambiguationData":[TD([[makeQuery(id+"F31.imprint","IMPRINT",EDGE,{"derivedFrom":sQuery(id+"F31.wireOp",EDGE,"E180")}),1.0]])]});
            var Q6;
            Q6=makeQuery(id+"F31.imprint","IMPRINT",FACE,{"disambiguationData":[TD([[makeQuery(id+"F31.imprint","IMPRINT",EDGE,{"derivedFrom":sQuery(id+"F31.wireOp",EDGE,"E181")}),1.0]])]});
            var Q7;
            Q7=makeQuery(id+"F31.imprint","IMPRINT",FACE,{"disambiguationData":[TD([[makeQuery(id+"F31.imprint","IMPRINT",EDGE,{"derivedFrom":sQuery(id+"F31.wireOp",EDGE,"E182")}),1.0]])]});
            var Q8;
            Q8=makeQuery(id+"F31.imprint","IMPRINT",FACE,{"disambiguationData":[TD([[makeQuery(id+"F31.imprint","IMPRINT",EDGE,{"derivedFrom":sQuery(id+"F31.wireOp",EDGE,"E183")}),1.0]])]});
            var Q9;
            Q9=makeQuery(id+"F31.imprint","IMPRINT",FACE,{"disambiguationData":[TD([[makeQuery(id+"F31.imprint","IMPRINT",EDGE,{"derivedFrom":sQuery(id+"F31.wireOp",EDGE,"E184")}),1.0]])]});
            var Q10;
            Q10=makeQuery(id+"F31.imprint","IMPRINT",FACE,{"disambiguationData":[TD([[makeQuery(id+"F31.imprint","IMPRINT",EDGE,{"derivedFrom":sQuery(id+"F31.wireOp",EDGE,"E185")}),1.0]])]});
            var Q11;
            Q11=makeQuery(id+"F31.imprint","IMPRINT",FACE,{"disambiguationData":[TD([[makeQuery(id+"F31.imprint","IMPRINT",EDGE,{"derivedFrom":sQuery(id+"F31.wireOp",EDGE,"E186")}),1.0]])]});
            var Q12;
            Q12=makeQuery(id+"F31.imprint","IMPRINT",FACE,{"disambiguationData":[TD([[makeQuery(id+"F31.imprint","IMPRINT",EDGE,{"derivedFrom":sQuery(id+"F31.wireOp",EDGE,"E187")}),1.0]])]});
            var Q13;
            Q13=makeQuery(id+"F31.imprint","IMPRINT",FACE,{"disambiguationData":[TD([[makeQuery(id+"F31.imprint","IMPRINT",EDGE,{"derivedFrom":sQuery(id+"F31.wireOp",EDGE,"E188")}),1.0]])]});
            var Q14;
            Q14=makeQuery(id+"F31.imprint","IMPRINT",FACE,{"disambiguationData":[TD([[makeQuery(id+"F31.imprint","IMPRINT",EDGE,{"derivedFrom":sQuery(id+"F31.wireOp",EDGE,"E189")}),1.0]])]});
            var Q15;
            Q15=makeQuery(id+"F1.opExtrude","CAP_FACE",FACE,{"disambiguationData":[OSD([sQuery(id+"F0.wireOp",EDGE,"E0")])],"isStart":true});
            extrude(context, id + "F32", {"entities" : qUnion([Q0, Q1, Q2, Q3, Q4, Q5, Q6, Q7, Q8, Q9, Q10, Q11, Q12, Q13, Q14]), "operationType" : NewBodyOperationType.REMOVE, "endBound" : BoundingType.UP_TO_SURFACE, "oppositeDirection" : true, "depth" : 25.4 * mm, "endBoundEntityFace" : qUnion([Q15]), "offsetDistance" : 25.4 * mm});
        }
        {
            var Q0;
            Q0=makeQuery(id+"F1.opExtrude","CAP_FACE",FACE,{"disambiguationData":[OSD([sQuery(id+"F0.wireOp",EDGE,"E0")])],"isStart":false});
            var sketch = newSketch(context, id + "F33", { "sketchPlane" : qUnion([Q0])});
            skLineSegment(sketch, "E190", {"start": v(-46.1, 15.97) * mm, "end": v(0, 0) * mm});
            skLineSegment(sketch, "E191", {"start": v(0, 0) * mm, "end": v(-43.8, 19.96) * mm});
            skLineSegment(sketch, "E192", {"start": v(-41.5, 23.95) * mm, "end": v(0, 0) * mm});
            skLineSegment(sketch, "E193", {"start": v(-39.19, 27.95) * mm, "end": v(0, 0) * mm});
            skLineSegment(sketch, "E194", {"start": v(-36.88, 31.94) * mm, "end": v(0, 0) * mm});
            skCircle(sketch, "E195", {"center": v(-46.1, 15.97) * mm, "radius": 1.9 * mm});
            skCircle(sketch, "E196", {"center": v(-43.8, 19.96) * mm, "radius": 1.9 * mm});
            skCircle(sketch, "E197", {"center": v(-41.5, 23.95) * mm, "radius": 1.9 * mm});
            skCircle(sketch, "E198", {"center": v(-39.19, 27.95) * mm, "radius": 1.9 * mm});
            skCircle(sketch, "E199", {"center": v(-36.88, 31.94) * mm, "radius": 1.9 * mm});
            skSolve(sketch);
        }
        {
            var Q0;
            Q0=makeQuery(id+"F33.imprint","IMPRINT",FACE,{"disambiguationData":[TD([[makeQuery(id+"F33.imprint","IMPRINT",EDGE,{"derivedFrom":sQuery(id+"F33.wireOp",EDGE,"E196")}),1.0]])]});
            var Q1;
            Q1=makeQuery(id+"F33.imprint","IMPRINT",FACE,{"disambiguationData":[TD([[makeQuery(id+"F33.imprint","IMPRINT",EDGE,{"derivedFrom":sQuery(id+"F33.wireOp",EDGE,"E195")}),1.0]])]});
            var Q2;
            Q2=makeQuery(id+"F33.imprint","IMPRINT",FACE,{"disambiguationData":[TD([[makeQuery(id+"F33.imprint","IMPRINT",EDGE,{"derivedFrom":sQuery(id+"F33.wireOp",EDGE,"E197")}),1.0]])]});
            var Q3;
            Q3=makeQuery(id+"F33.imprint","IMPRINT",FACE,{"disambiguationData":[TD([[makeQuery(id+"F33.imprint","IMPRINT",EDGE,{"derivedFrom":sQuery(id+"F33.wireOp",EDGE,"E198")}),1.0]])]});
            var Q4;
            Q4=makeQuery(id+"F33.imprint","IMPRINT",FACE,{"disambiguationData":[TD([[makeQuery(id+"F33.imprint","IMPRINT",EDGE,{"derivedFrom":sQuery(id+"F33.wireOp",EDGE,"E199")}),1.0]])]});
            var Q5;
            Q5=makeQuery(id+"F1.opExtrude","CAP_FACE",FACE,{"disambiguationData":[OSD([sQuery(id+"F0.wireOp",EDGE,"E0")])],"isStart":true});
            extrude(context, id + "F34", {"entities" : qUnion([Q0, Q1, Q2, Q3, Q4]), "operationType" : NewBodyOperationType.REMOVE, "endBound" : BoundingType.UP_TO_SURFACE, "oppositeDirection" : true, "depth" : 25.4 * mm, "endBoundEntityFace" : qUnion([Q5]), "offsetDistance" : 25.4 * mm});
        }
    });
